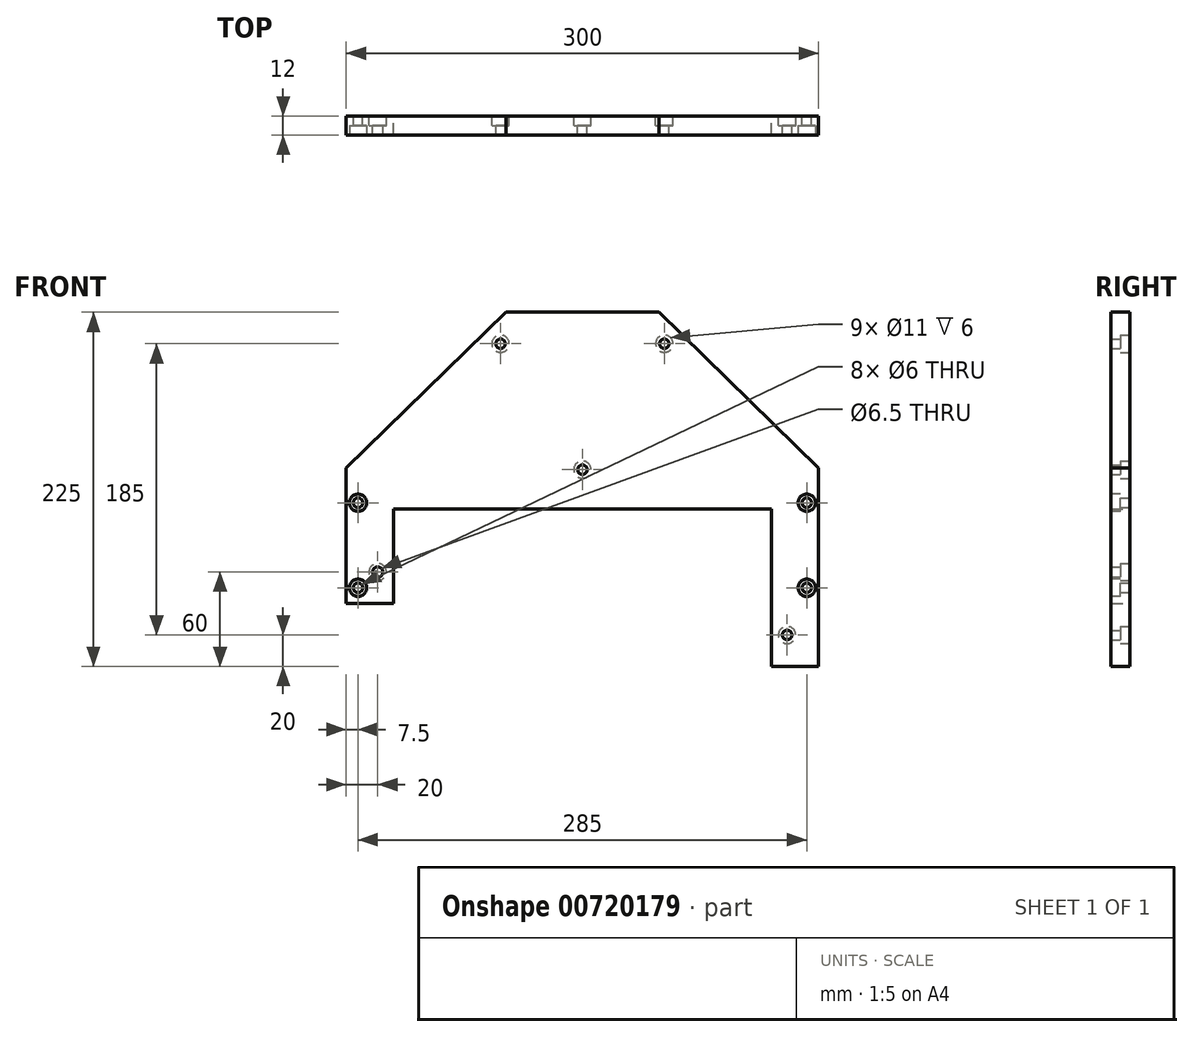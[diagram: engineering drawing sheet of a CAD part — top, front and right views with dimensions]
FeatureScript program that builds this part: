
annotation { "Feature Type Name" : "Feature", "Feature Type Description" : "" }
export const myFeature = defineFeature(function(context is Context, id is Id, definition is map)
    precondition{}
    {
        {
            var Q0;
            Q0=qCreatedBy(makeId("Front.planeOp"),FACE);
            var sketch = newSketch(context, id + "F0", { "sketchPlane" : qUnion([Q0])});
            skLineSegment(sketch, "E0", {"start": v(-300, -185) * mm, "end": v(-300, -99) * mm});
            skLineSegment(sketch, "E1", {"start": v(-300, -99) * mm, "end": v(-198.5, 0) * mm});
            skLineSegment(sketch, "E2", {"start": v(-198.5, 0) * mm, "end": v(-101.5, 0) * mm});
            skLineSegment(sketch, "E3", {"start": v(-101.5, 0) * mm, "end": v(0, -99) * mm});
            skLineSegment(sketch, "E4", {"start": v(-300, -185) * mm, "end": v(-270, -185) * mm});
            skLineSegment(sketch, "E5", {"start": v(-270, -185) * mm, "end": v(-270, -125) * mm});
            skLineSegment(sketch, "E6", {"start": v(-270, -125) * mm, "end": v(-30, -125) * mm});
            skLineSegment(sketch, "E7", {"start": v(-30, -125) * mm, "end": v(-30, -225) * mm});
            skLineSegment(sketch, "E8", {"start": v(-30, -225) * mm, "end": v(0, -225) * mm});
            skLineSegment(sketch, "E9", {"start": v(0, -225) * mm, "end": v(0, -99) * mm});
            skLineSegment(sketch, "E10", {"start": v(-300, -99) * mm, "end": v(0, -99) * mm, "construction": true});
            skLineSegment(sketch, "E11", {"start": v(-150, -125) * mm, "end": v(-150, 6.86) * mm, "construction": true});
            skCircle(sketch, "E12", {"center": v(-292.5, -175) * mm, "radius": 3 * mm});
            skCircle(sketch, "E13", {"center": v(-292.5, -121) * mm, "radius": 3 * mm});
            skCircle(sketch, "E14", {"center": v(-280, -165) * mm, "radius": 3.25 * mm});
            skCircle(sketch, "E15", {"center": v(-7.5, -121) * mm, "radius": 3 * mm});
            skCircle(sketch, "E16", {"center": v(-7.5, -175) * mm, "radius": 3 * mm});
            skPoint(sketch, "E16.centerSnap0", {"position": v(-30, -175) * mm});
            skCircle(sketch, "E17", {"center": v(-20, -205) * mm, "radius": 3 * mm});
            skCircle(sketch, "E18", {"center": v(-202, -20) * mm, "radius": 3 * mm});
            skCircle(sketch, "E19", {"center": v(-98, -20) * mm, "radius": 3 * mm});
            skCircle(sketch, "E20", {"center": v(-150, -100) * mm, "radius": 3 * mm});
            skSolve(sketch);
        }
        {
            var Q0;
            Q0=makeQuery(id+"F0.imprint","IMPRINT",FACE,{"disambiguationData":[TD([[makeQuery(id+"F0.imprint","IMPRINT",EDGE,{"derivedFrom":sQuery(id+"F0.wireOp",EDGE,"E0")}),-1.0]])]});
            extrude(context, id + "F1", {"entities" : qUnion([Q0]), "depth" : 12 * mm, "offsetDistance" : 25 * mm});
        }
        {
            var Q0;
            Q0=makeQuery(id+"F1.opExtrude","CAP_FACE",FACE,{"disambiguationData":[OSD([sQuery(id+"F0.wireOp",EDGE,"E0"),sQuery(id+"F0.wireOp",EDGE,"E1"),sQuery(id+"F0.wireOp",EDGE,"E2"),sQuery(id+"F0.wireOp",EDGE,"E3"),sQuery(id+"F0.wireOp",EDGE,"E4"),sQuery(id+"F0.wireOp",EDGE,"E5"),sQuery(id+"F0.wireOp",EDGE,"E6"),sQuery(id+"F0.wireOp",EDGE,"E7"),sQuery(id+"F0.wireOp",EDGE,"E8"),sQuery(id+"F0.wireOp",EDGE,"E9"),sQuery(id+"F0.wireOp",EDGE,"E12"),sQuery(id+"F0.wireOp",EDGE,"E13"),sQuery(id+"F0.wireOp",EDGE,"E14"),sQuery(id+"F0.wireOp",EDGE,"E15"),sQuery(id+"F0.wireOp",EDGE,"E16"),sQuery(id+"F0.wireOp",EDGE,"E17"),sQuery(id+"F0.wireOp",EDGE,"E18"),sQuery(id+"F0.wireOp",EDGE,"E19")])],"isStart":false});
            var sketch = newSketch(context, id + "F2", { "sketchPlane" : qUnion([Q0])});
            skCircle(sketch, "E21", {"center": v(-292.5, -175) * mm, "radius": 5.5 * mm});
            skCircle(sketch, "E22", {"center": v(-292.5, -121) * mm, "radius": 5.5 * mm});
            skCircle(sketch, "E23", {"center": v(-7.5, -175) * mm, "radius": 5.5 * mm});
            skCircle(sketch, "E24", {"center": v(-7.5, -121) * mm, "radius": 5.5 * mm});
            skSolve(sketch);
        }
        {
            var Q0;
            Q0 = qSketchRegion(id + "F2", true);
            extrude(context, id + "F3", {"entities" : qUnion([Q0]), "operationType" : NewBodyOperationType.REMOVE, "oppositeDirection" : true, "depth" : 6 * mm, "offsetDistance" : 25 * mm});
        }
        {
            var Q0;
            Q0=makeQuery(id+"F1.opExtrude","CAP_FACE",FACE,{"disambiguationData":[OSD([sQuery(id+"F0.wireOp",EDGE,"E0"),sQuery(id+"F0.wireOp",EDGE,"E1"),sQuery(id+"F0.wireOp",EDGE,"E2"),sQuery(id+"F0.wireOp",EDGE,"E3"),sQuery(id+"F0.wireOp",EDGE,"E4"),sQuery(id+"F0.wireOp",EDGE,"E5"),sQuery(id+"F0.wireOp",EDGE,"E6"),sQuery(id+"F0.wireOp",EDGE,"E7"),sQuery(id+"F0.wireOp",EDGE,"E8"),sQuery(id+"F0.wireOp",EDGE,"E9"),sQuery(id+"F0.wireOp",EDGE,"E12"),sQuery(id+"F0.wireOp",EDGE,"E13"),sQuery(id+"F0.wireOp",EDGE,"E14"),sQuery(id+"F0.wireOp",EDGE,"E15"),sQuery(id+"F0.wireOp",EDGE,"E16"),sQuery(id+"F0.wireOp",EDGE,"E17"),sQuery(id+"F0.wireOp",EDGE,"E18"),sQuery(id+"F0.wireOp",EDGE,"E19")])],"isStart":true});
            var sketch = newSketch(context, id + "F4", { "sketchPlane" : qUnion([Q0])});
            skCircle(sketch, "E25", {"center": v(20, -205) * mm, "radius": 5.5 * mm});
            skCircle(sketch, "E26", {"center": v(280, -165) * mm, "radius": 5.5 * mm});
            skCircle(sketch, "E27", {"center": v(98, -20) * mm, "radius": 5.5 * mm});
            skCircle(sketch, "E28", {"center": v(202, -20) * mm, "radius": 5.5 * mm});
            skCircle(sketch, "E29", {"center": v(150, -100) * mm, "radius": 5.5 * mm});
            skSolve(sketch);
        }
        {
            var Q0;
            Q0 = qSketchRegion(id + "F4", true);
            extrude(context, id + "F5", {"entities" : qUnion([Q0]), "operationType" : NewBodyOperationType.REMOVE, "oppositeDirection" : true, "depth" : 6 * mm, "offsetDistance" : 25 * mm});
        }
    });
